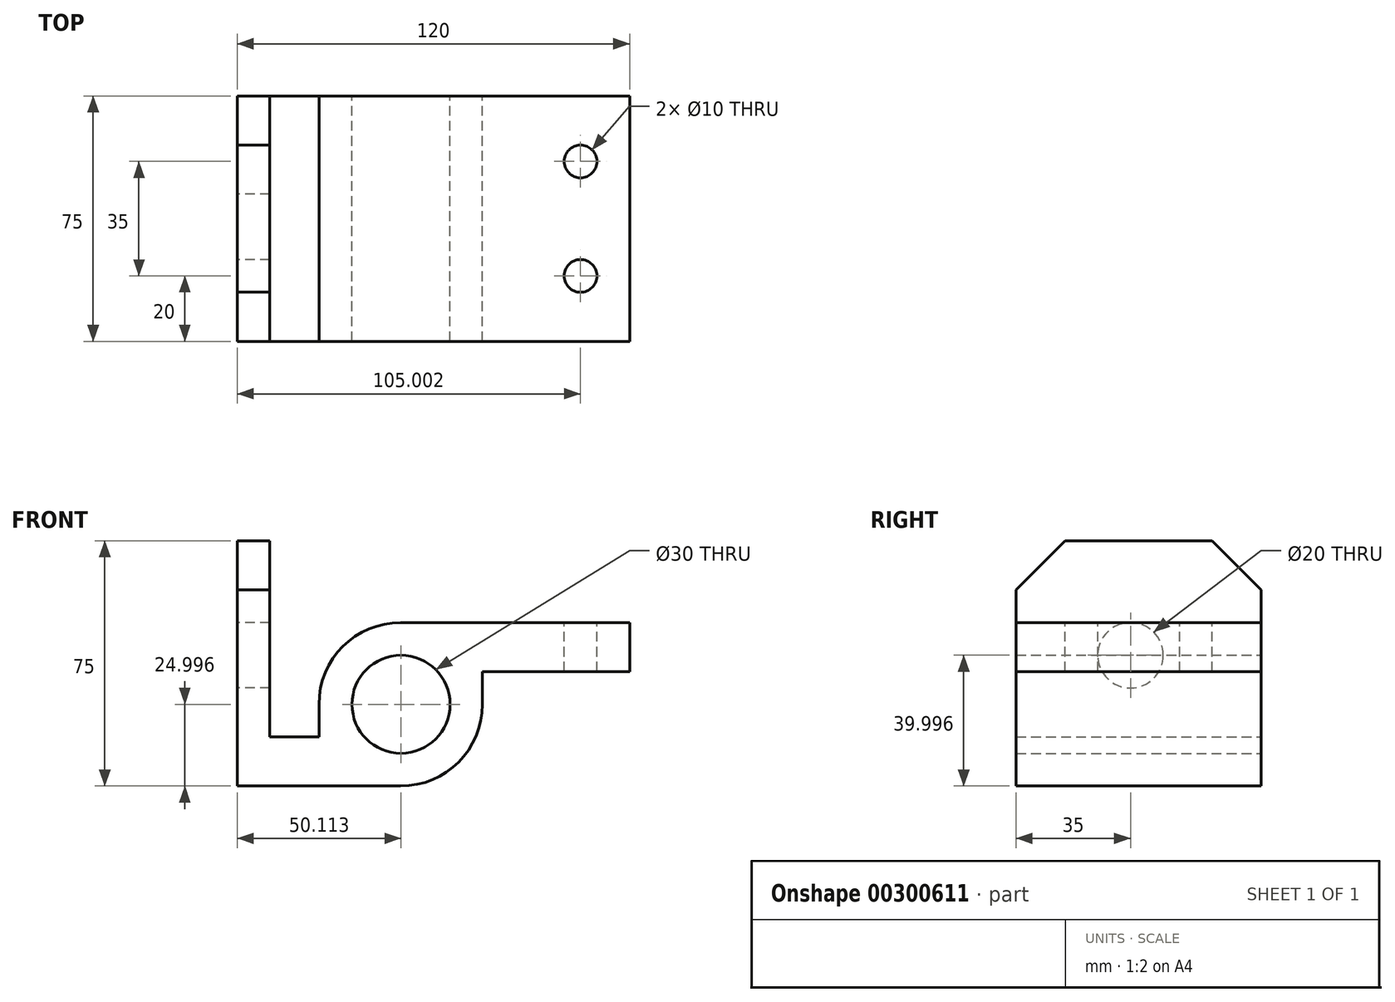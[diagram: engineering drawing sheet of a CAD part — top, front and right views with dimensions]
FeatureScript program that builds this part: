
annotation { "Feature Type Name" : "Feature", "Feature Type Description" : "" }
export const myFeature = defineFeature(function(context is Context, id is Id, definition is map)
    precondition{}
    {
        {
            var Q0;
            Q0=qCreatedBy(makeId("Front.planeOp"),FACE);
            var sketch = newSketch(context, id + "F0", { "sketchPlane" : qUnion([Q0])});
            skLineSegment(sketch, "E0", {"start": v(80.72, 39.36) * mm, "end": v(80.72, 24.36) * mm});
            skLineSegment(sketch, "E1", {"start": v(80.72, 39.36) * mm, "end": v(10.72, 39.36) * mm});
            skLineSegment(sketch, "E2", {"start": v(80.72, 24.36) * mm, "end": v(35.72, 24.36) * mm});
            skLineSegment(sketch, "E3", {"start": v(35.72, 14.36) * mm, "end": v(35.72, 24.36) * mm});
            skLineSegment(sketch, "E4", {"start": v(10.72, -10.64) * mm, "end": v(-39.28, -10.64) * mm});
            skLineSegment(sketch, "E5", {"start": v(-14.28, 14.36) * mm, "end": v(-14.28, 4.36) * mm});
            skLineSegment(sketch, "E6", {"start": v(-14.28, 4.36) * mm, "end": v(-29.28, 4.36) * mm});
            skLineSegment(sketch, "E7", {"start": v(-29.28, 4.36) * mm, "end": v(-29.28, 64.36) * mm});
            skLineSegment(sketch, "E8", {"start": v(-39.28, -10.64) * mm, "end": v(-39.28, 64.36) * mm});
            skLineSegment(sketch, "E9", {"start": v(-39.28, 64.36) * mm, "end": v(-29.28, 64.36) * mm});
            skCircle(sketch, "E10", {"center": v(10.83, 14.36) * mm, "radius": 15 * mm});
            skPoint(sketch, "E11.visualSharp", {"position": v(-14.28, 39.36) * mm});
            skArc(sketch, "E11.filletArc", {"start": v(10.72, 39.36) * mm, "mid": v(-6.96, 32.03) * mm, "end": v(-14.28, 14.36) * mm});
            skPoint(sketch, "E12.visualSharp", {"position": v(35.72, -10.64) * mm});
            skArc(sketch, "E12.filletArc", {"start": v(10.72, -10.64) * mm, "mid": v(28.4, -3.32) * mm, "end": v(35.72, 14.36) * mm});
            skSolve(sketch);
        }
        {
            var Q0;
            Q0=makeQuery(id+"F0.imprint","IMPRINT",FACE,{"disambiguationData":[TD([[makeQuery(id+"F0.imprint","IMPRINT",EDGE,{"derivedFrom":sQuery(id+"F0.wireOp",EDGE,"E0")}),-1.0]])]});
            extrude(context, id + "F1", {"entities" : qUnion([Q0]), "depth" : 75 * mm});
        }
        {
            var Q0;
            Q0=makeQuery(id+"F1.opExtrude","SWEPT_FACE",FACE,{"disambiguationData":[OSD([sQuery(id+"F0.wireOp",EDGE,"E1")])]});
            var sketch = newSketch(context, id + "F2", { "sketchPlane" : qUnion([Q0])});
            skCircle(sketch, "E13", {"center": v(65.72, -20) * mm, "radius": 5 * mm});
            skCircle(sketch, "E14", {"center": v(65.72, -55) * mm, "radius": 5 * mm});
            skSolve(sketch);
        }
        {
            var Q0;
            Q0=makeQuery(id+"F2.imprint","IMPRINT",FACE,{"disambiguationData":[TD([[makeQuery(id+"F2.imprint","IMPRINT",EDGE,{"derivedFrom":sQuery(id+"F2.wireOp",EDGE,"E13")}),1.0]])]});
            var Q1;
            Q1=makeQuery(id+"F2.imprint","IMPRINT",FACE,{"disambiguationData":[TD([[makeQuery(id+"F2.imprint","IMPRINT",EDGE,{"derivedFrom":sQuery(id+"F2.wireOp",EDGE,"E14")}),1.0]])]});
            extrude(context, id + "F3", {"entities" : qUnion([Q0, Q1]), "operationType" : NewBodyOperationType.REMOVE, "oppositeDirection" : true, "depth" : 25 * mm});
        }
        {
            var Q0;
            Q0=makeQuery(id+"F1.opExtrude","SWEPT_FACE",FACE,{"disambiguationData":[OSD([sQuery(id+"F0.wireOp",EDGE,"E8")])]});
            var sketch = newSketch(context, id + "F4", { "sketchPlane" : qUnion([Q0])});
            skCircle(sketch, "E15", {"center": v(40, 29.36) * mm, "radius": 10 * mm});
            skLineSegment(sketch, "E16", {"start": v(15, 64.36) * mm, "end": v(0, 49.36) * mm});
            skLineSegment(sketch, "E17", {"start": v(60, 64.36) * mm, "end": v(75, 49.36) * mm});
            skSolve(sketch);
        }
        {
            var Q0;
            {var subQ0=sQuery(id+"F4.wireOp",EDGE,"E16");Q0=makeQuery(id+"F4.imprint","IMPRINT",FACE,{"disambiguationData":[TD([[makeQuery(id+"F4.imprint","IMPRINT",EDGE,{"derivedFrom":subQ0}),-1.0]])]});}
            var Q1;
            {var subQ0=sQuery(id+"F4.wireOp",EDGE,"E17");Q1=makeQuery(id+"F4.imprint","IMPRINT",FACE,{"disambiguationData":[TD([[makeQuery(id+"F4.imprint","IMPRINT",EDGE,{"derivedFrom":subQ0}),1.0]])]});}
            var Q2;
            Q2=makeQuery(id+"F4.imprint","IMPRINT",FACE,{"disambiguationData":[TD([[makeQuery(id+"F4.imprint","IMPRINT",EDGE,{"derivedFrom":sQuery(id+"F4.wireOp",EDGE,"E15")}),1.0]])]});
            extrude(context, id + "F5", {"entities" : qUnion([Q0, Q1, Q2]), "operationType" : NewBodyOperationType.REMOVE, "oppositeDirection" : true, "depth" : 25 * mm});
        }
    });
